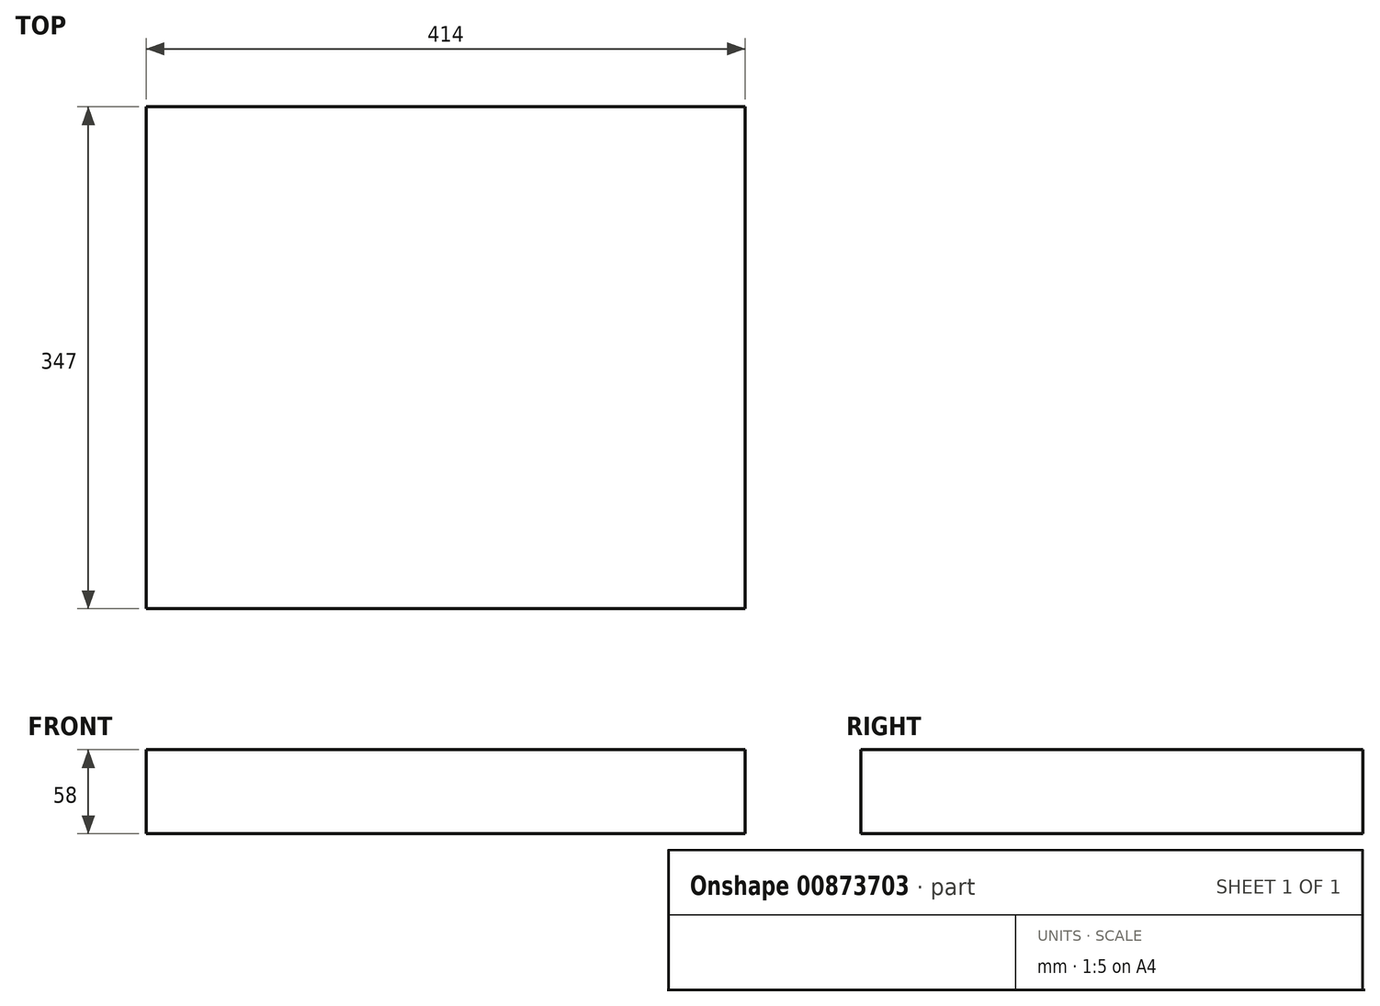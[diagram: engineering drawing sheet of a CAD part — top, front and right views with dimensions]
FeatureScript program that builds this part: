
annotation { "Feature Type Name" : "Feature", "Feature Type Description" : "" }
export const myFeature = defineFeature(function(context is Context, id is Id, definition is map)
    precondition{}
    {
        {
            var Q0;
            Q0=qCreatedBy(makeId("Top.planeOp"),FACE);
            var sketch = newSketch(context, id + "F0", { "sketchPlane" : qUnion([Q0])});
            skLineSegment(sketch, "E0.bottom", {"start": v(207, -173.5) * mm, "end": v(-207, -173.5) * mm});
            skLineSegment(sketch, "E0.top", {"start": v(207, 173.5) * mm, "end": v(-207, 173.5) * mm});
            skLineSegment(sketch, "E0.left", {"start": v(207, -173.5) * mm, "end": v(207, 173.5) * mm});
            skLineSegment(sketch, "E0.right", {"start": v(-207, -173.5) * mm, "end": v(-207, 173.5) * mm});
            skPoint(sketch, "E0.middle", {"position": v(0, 0) * mm});
            skSolve(sketch);
        }
        {
            var Q0;
            Q0=makeQuery(id+"F0.imprint","IMPRINT",FACE,{"disambiguationData":[TD([[makeQuery(id+"F0.imprint","IMPRINT",EDGE,{"derivedFrom":sQuery(id+"F0.wireOp",EDGE,"E0.bottom")}),-1.0]])]});
            extrude(context, id + "F1", {"entities" : qUnion([Q0]), "oppositeDirection" : true, "depth" : 58 * mm, "offsetDistance" : 25 * mm});
        }
    });
